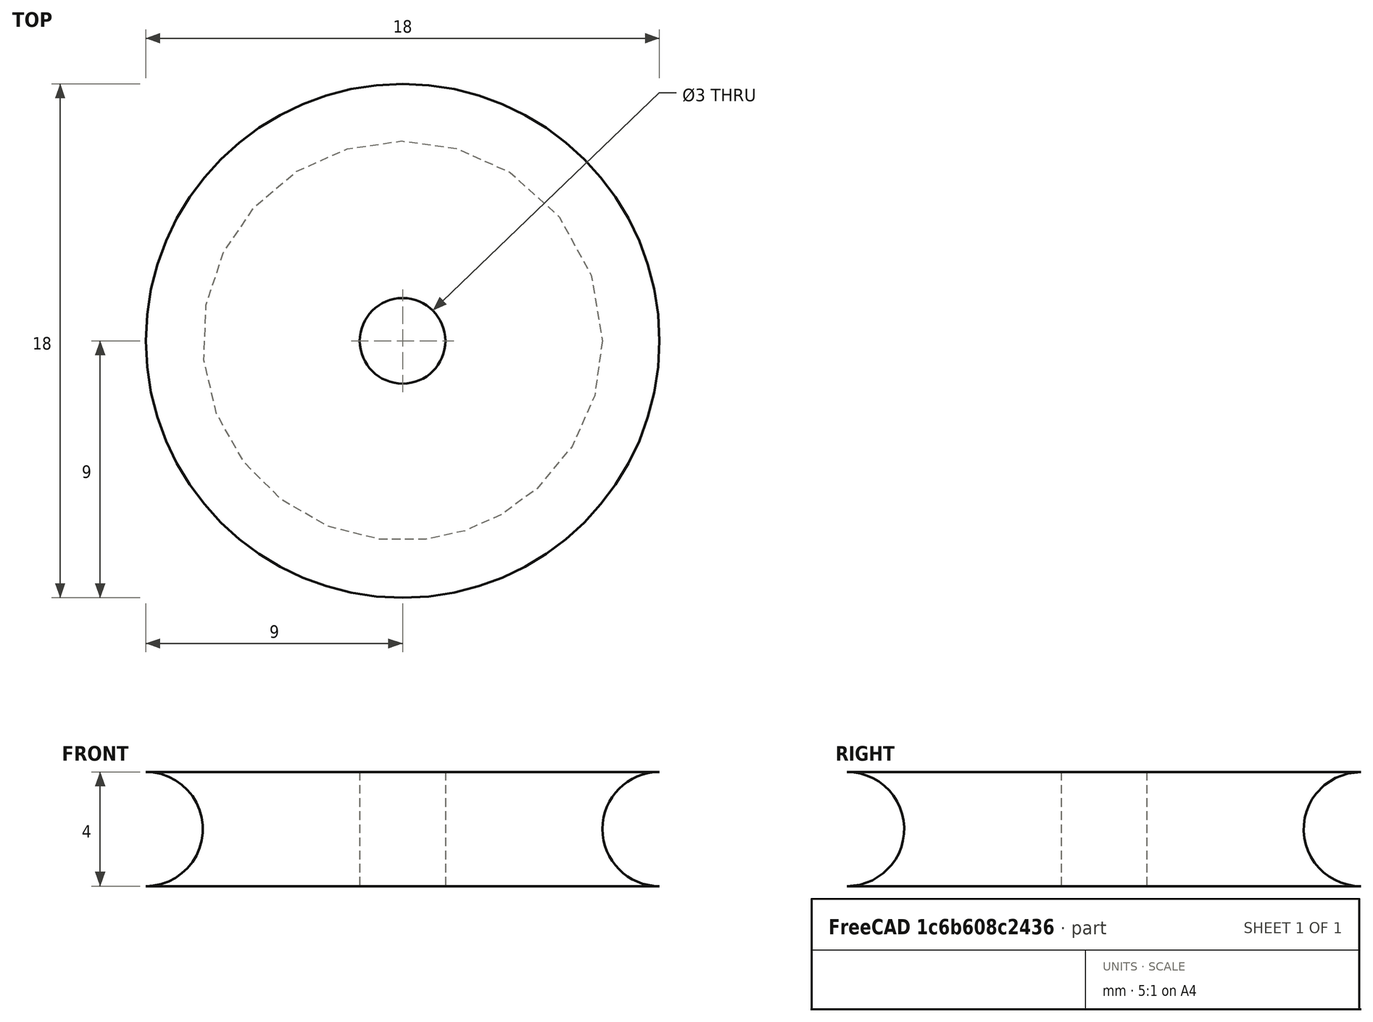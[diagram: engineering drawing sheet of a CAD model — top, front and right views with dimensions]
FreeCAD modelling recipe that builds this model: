
FCSTD DOCUMENT  (FreeCAD 0.18R16110 (Git))
Label: roller3
License: All rights reserved
LicenseURL: http://en.wikipedia.org/wiki/All_rights_reserved
objects: Sketcher::SketchObject×1, PartDesign::Revolution×1, PartDesign::Body×1
note: 4 computed .brp shape members not serialized (recipe doc carries the construction recipe); baked Part::Feature solids carry a one-line shape summary decoded from their .brp

FEATURE [Sketcher::SketchObject] Sketch
  MapMode = 5
  Placement = pos=(0,0,0) rot=(1,0,0;1.5708rad)
  Support = -> [XZ_Plane]
  sketch-geometry (4):
    g0: LineSegment StartX=1.5 StartY=0 StartZ=0 EndX=9 EndY=0 EndZ=0
    g1: LineSegment StartX=9 StartY=4 StartZ=0 EndX=1.5 EndY=4 EndZ=0
    g2: LineSegment StartX=1.5 StartY=4 StartZ=0 EndX=1.5 EndY=0 EndZ=0
    g3: ArcOfCircle CenterX=9.00002 CenterY=2 CenterZ=0 NormalX=0 NormalY=0 NormalZ=1 AngleXU=0 Radius=2 StartAngle=1.5708 EndAngle=4.71238
  constraints (13):
    c: Coincident(g1,g2)
    c: Coincident(g2,g0)
    c: Vertical(g2)
    c: Horizontal(g1)
    c: Horizontal(g0)
    c: PointOnObject(g0,g-1)
    c: Distance(g-1,g0) = 1.5
    c: DistanceY(g-1,g1) = 4
    c: DistanceX(g-1,g0) = 9
    c: Equal(g1,g0)
    c: Coincident(g3,g0)
    c: Coincident(g3,g1)
    c: Radius(g3) = 2
FEATURE [PartDesign::Revolution] Revolution
  Angle = 360
  Axis = (0,-2e-16,1)
  Base = (0,0,0)
  Placement = pos=(0,0,0) rot=(1,0,0;1.5708rad)
  Profile = -> Sketch
  ReferenceAxis = -> Sketch [V_Axis]
  Reversed = true
FEATURE [PartDesign::Body] Body
  Group = -> [Sketch,Revolution]
  Origin = -> Origin
  Tip = -> Revolution
